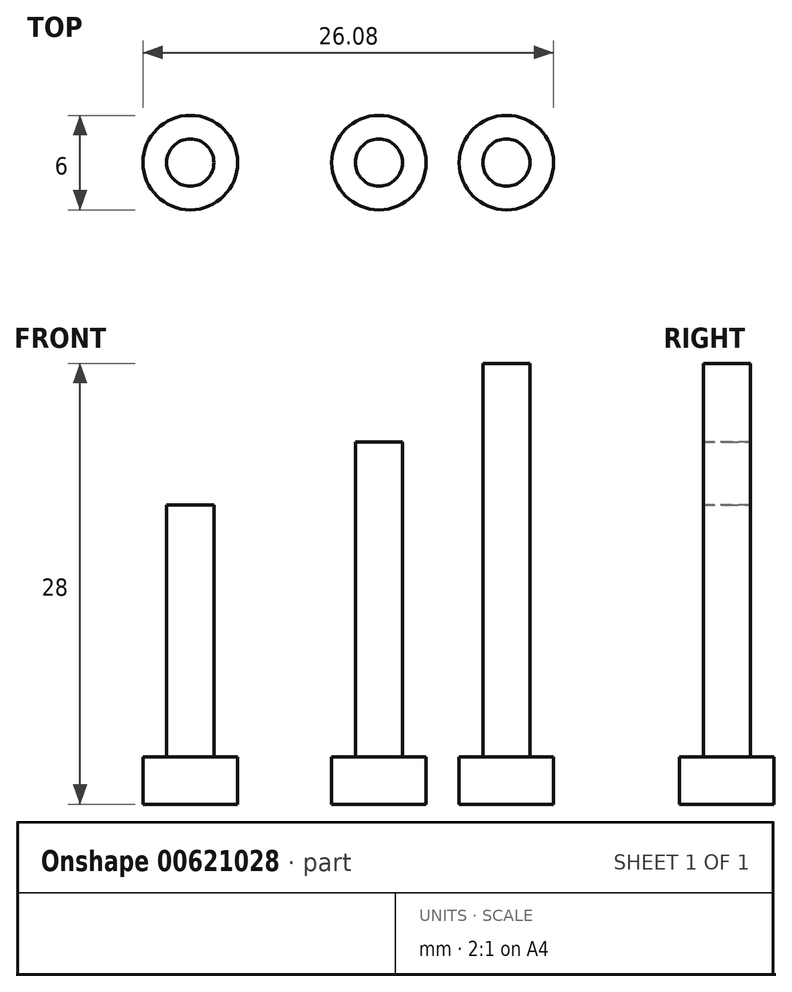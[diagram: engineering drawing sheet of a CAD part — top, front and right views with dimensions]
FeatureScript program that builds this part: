
annotation { "Feature Type Name" : "Feature", "Feature Type Description" : "" }
export const myFeature = defineFeature(function(context is Context, id is Id, definition is map)
    precondition{}
    {
        {
            var Q0;
            Q0=qCreatedBy(makeId("Front.planeOp"),FACE);
            var sketch = newSketch(context, id + "F0", { "sketchPlane" : qUnion([Q0])});
            skLineSegment(sketch, "E0", {"start": v(-43.65, 0) * mm, "end": v(-43.65, 23) * mm});
            skLineSegment(sketch, "E1", {"start": v(-43.65, 23) * mm, "end": v(-45.15, 23) * mm});
            skLineSegment(sketch, "E2", {"start": v(-45.15, 23) * mm, "end": v(-45.15, 3) * mm});
            skLineSegment(sketch, "E3", {"start": v(-45.15, 3) * mm, "end": v(-46.65, 3) * mm});
            skLineSegment(sketch, "E4", {"start": v(-46.65, 3) * mm, "end": v(-46.65, 0) * mm});
            skLineSegment(sketch, "E5", {"start": v(-46.65, 0) * mm, "end": v(-43.65, 0) * mm});
            skLineSegment(sketch, "E6", {"start": v(-38.55, 0) * mm, "end": v(-38.55, 3) * mm});
            skLineSegment(sketch, "E7", {"start": v(-38.55, 3) * mm, "end": v(-37.05, 3) * mm});
            skLineSegment(sketch, "E8", {"start": v(-37.05, 3) * mm, "end": v(-37.05, 28) * mm});
            skLineSegment(sketch, "E9", {"start": v(-37.05, 28) * mm, "end": v(-35.55, 28) * mm});
            skLineSegment(sketch, "E10", {"start": v(-35.55, 28) * mm, "end": v(-35.55, 0) * mm});
            skLineSegment(sketch, "E11", {"start": v(-35.55, 0) * mm, "end": v(-38.55, 0) * mm});
            skLineSegment(sketch, "E12", {"start": v(-58.63, 0) * mm, "end": v(-55.63, 0) * mm});
            skLineSegment(sketch, "E13", {"start": v(-55.63, 0) * mm, "end": v(-55.63, 19) * mm});
            skLineSegment(sketch, "E14", {"start": v(-55.63, 19) * mm, "end": v(-57.13, 19) * mm});
            skLineSegment(sketch, "E15", {"start": v(-57.13, 19) * mm, "end": v(-57.13, 3) * mm});
            skLineSegment(sketch, "E16", {"start": v(-57.13, 3) * mm, "end": v(-58.63, 3) * mm});
            skLineSegment(sketch, "E17", {"start": v(-58.63, 3) * mm, "end": v(-58.63, 0) * mm});
            skSolve(sketch);
        }
        {
            var Q0;
            Q0=makeQuery(id+"F0.imprint","IMPRINT",FACE,{"disambiguationData":[TD([[makeQuery(id+"F0.imprint","IMPRINT",EDGE,{"derivedFrom":sQuery(id+"F0.wireOp",EDGE,"E0")}),1.0]])]});
            var Q1;
            Q1=sQuery(id+"F0.wireOp",EDGE,"E0");
            revolve(context, id + "F1", {"entities" : qUnion([Q0]), "axis" : qUnion([Q1]), "revolveType" : RevolveType.FULL});
        }
        {
            var Q0;
            Q0=makeQuery(id+"F0.imprint","IMPRINT",FACE,{"disambiguationData":[TD([[makeQuery(id+"F0.imprint","IMPRINT",EDGE,{"derivedFrom":sQuery(id+"F0.wireOp",EDGE,"E6")}),-1.0]])]});
            var Q1;
            Q1=sQuery(id+"F0.wireOp",EDGE,"E10");
            revolve(context, id + "F2", {"entities" : qUnion([Q0]), "axis" : qUnion([Q1]), "revolveType" : RevolveType.FULL});
        }
        {
            var Q0;
            Q0=makeQuery(id+"F0.imprint","IMPRINT",FACE,{"disambiguationData":[TD([[makeQuery(id+"F0.imprint","IMPRINT",EDGE,{"derivedFrom":sQuery(id+"F0.wireOp",EDGE,"E12")}),1.0]])]});
            var Q1;
            Q1=sQuery(id+"F0.wireOp",EDGE,"E13");
            revolve(context, id + "F3", {"entities" : qUnion([Q0]), "axis" : qUnion([Q1]), "revolveType" : RevolveType.FULL});
        }
    });
